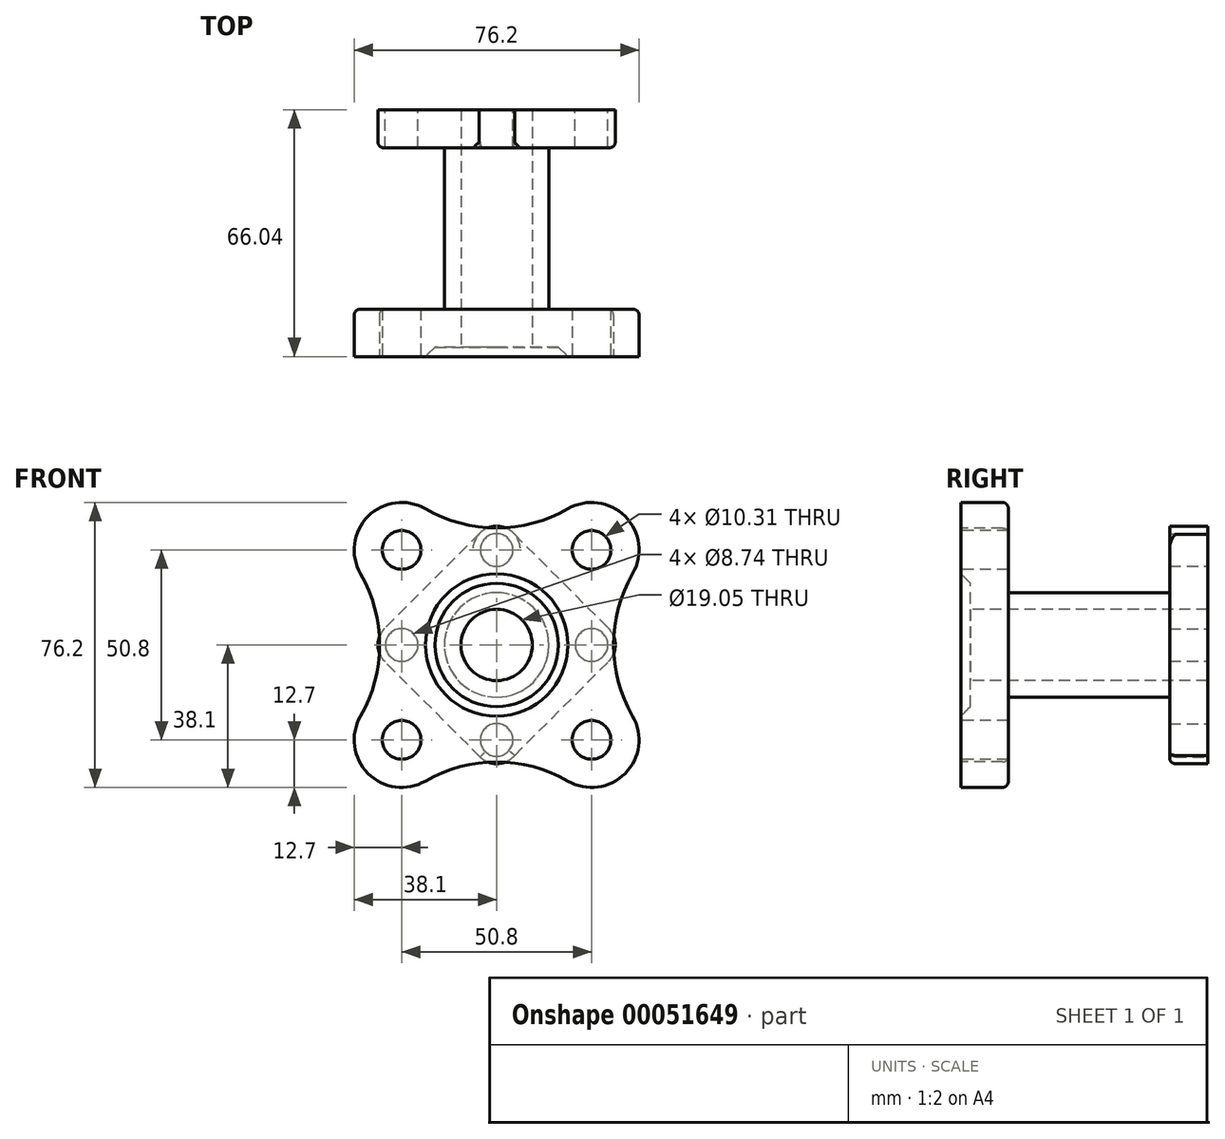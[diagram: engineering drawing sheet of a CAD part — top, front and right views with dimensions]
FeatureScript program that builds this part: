
annotation { "Feature Type Name" : "Feature", "Feature Type Description" : "" }
export const myFeature = defineFeature(function(context is Context, id is Id, definition is map)
    precondition{}
    {
        {
            var Q0;
            Q0=qCreatedBy(makeId("Front.planeOp"),FACE);
            var sketch = newSketch(context, id + "F0", { "sketchPlane" : qUnion([Q0])});
            skLineSegment(sketch, "E0.bottom", {"start": v(-25.4, 25.4) * mm, "end": v(25.4, 25.4) * mm, "construction": true});
            skLineSegment(sketch, "E0.top", {"start": v(-25.4, -25.4) * mm, "end": v(25.4, -25.4) * mm, "construction": true});
            skLineSegment(sketch, "E0.left", {"start": v(-25.4, 25.4) * mm, "end": v(-25.4, -25.4) * mm, "construction": true});
            skLineSegment(sketch, "E0.right", {"start": v(25.4, 25.4) * mm, "end": v(25.4, -25.4) * mm, "construction": true});
            skArc(sketch, "E1", {"start": v(19.05, -36.4) * mm, "mid": v(34.38, -34.38) * mm, "end": v(36.4, -19.05) * mm});
            skArc(sketch, "E2", {"start": v(-36.4, -19.05) * mm, "mid": v(-34.38, -34.38) * mm, "end": v(-19.05, -36.4) * mm});
            skCircle(sketch, "E3", {"center": v(-25.4, 25.4) * mm, "radius": 50.8 * mm, "construction": true});
            skCircle(sketch, "E4", {"center": v(-25.4, -25.4) * mm, "radius": 50.8 * mm, "construction": true});
            skArc(sketch, "E5", {"start": v(-36.4, -19.05) * mm, "mid": v(-31.3, 0) * mm, "end": v(-36.4, 19.05) * mm});
            skArc(sketch, "E6.MirrorCS", {"start": v(36.4, -19.05) * mm, "mid": v(31.3, 0) * mm, "end": v(36.4, 19.05) * mm});
            skCircle(sketch, "E7", {"center": v(25.4, 25.4) * mm, "radius": 50.8 * mm, "construction": true});
            skArc(sketch, "E8", {"start": v(-19.05, 36.4) * mm, "mid": v(0, 31.3) * mm, "end": v(19.05, 36.4) * mm});
            skArc(sketch, "E9.MirrorCS", {"start": v(-19.05, -36.4) * mm, "mid": v(0, -31.3) * mm, "end": v(19.05, -36.4) * mm});
            skArc(sketch, "E10.trimOffspring", {"start": v(-19.05, 36.4) * mm, "mid": v(-34.38, 34.38) * mm, "end": v(-36.4, 19.05) * mm});
            skArc(sketch, "E11.trimOffspring", {"start": v(36.4, 19.05) * mm, "mid": v(34.38, 34.38) * mm, "end": v(19.05, 36.4) * mm});
            skCircle(sketch, "E12", {"center": v(-25.4, 25.4) * mm, "radius": 5.16 * mm});
            skCircle(sketch, "E13", {"center": v(25.4, 25.4) * mm, "radius": 5.16 * mm});
            skCircle(sketch, "E14", {"center": v(-25.4, -25.4) * mm, "radius": 5.16 * mm});
            skCircle(sketch, "E15", {"center": v(25.4, -25.4) * mm, "radius": 5.16 * mm});
            skSolve(sketch);
        }
        {
            var Q0;
            Q0=makeQuery(id+"F0.imprint","IMPRINT",FACE,{"disambiguationData":[TD([[makeQuery(id+"F0.imprint","IMPRINT",EDGE,{"derivedFrom":sQuery(id+"F0.wireOp",EDGE,"E1")}),1.0]])]});
            extrude(context, id + "F1", {"entities" : qUnion([Q0]), "oppositeDirection" : true, "depth" : 12.7 * mm});
        }
        {
            var Q0;
            Q0=qCreatedBy(makeId("Front.planeOp"),FACE);
            cPlane(context, id + "F2", {"entities" : qUnion([Q0]), "cplaneType" : CPlaneType.OFFSET, "offset" : 66.04 * mm, "oppositeDirection" : true, "width" : 152.4 * mm, "height" : 152.4 * mm});
        }
        {
            var Q0;
            Q0=qCreatedBy(id+"F2.planeOp",FACE);
            var sketch = newSketch(context, id + "F3", { "sketchPlane" : qUnion([Q0])});
            skArc(sketch, "E16", {"start": v(4.78, 29.58) * mm, "mid": v(0.1, 31.75) * mm, "end": v(-4.64, 29.74) * mm});
            skArc(sketch, "E17", {"start": v(-29.89, 4.5) * mm, "mid": v(-31.75, 0) * mm, "end": v(-29.9, -4.5) * mm});
            skArc(sketch, "E18", {"start": v(-4.4, -29.97) * mm, "mid": v(0.29, -31.74) * mm, "end": v(4.8, -29.55) * mm});
            skArc(sketch, "E19", {"start": v(29.89, -4.5) * mm, "mid": v(31.75, 0) * mm, "end": v(29.89, 4.5) * mm});
            skLineSegment(sketch, "E20", {"start": v(-4.64, 29.74) * mm, "end": v(-29.89, 4.5) * mm});
            skLineSegment(sketch, "E21", {"start": v(-4.4, -29.97) * mm, "end": v(-29.9, -4.5) * mm});
            skLineSegment(sketch, "E22", {"start": v(4.78, 29.58) * mm, "end": v(29.89, 4.5) * mm});
            skLineSegment(sketch, "E23", {"start": v(4.8, -29.55) * mm, "end": v(29.89, -4.5) * mm});
            skSolve(sketch);
        }
        {
            var Q0;
            Q0=makeQuery(id+"F3.imprint","IMPRINT",FACE,{"disambiguationData":[TD([[makeQuery(id+"F3.imprint","IMPRINT",EDGE,{"derivedFrom":sQuery(id+"F3.wireOp",EDGE,"E16")}),1.0]])]});
            extrude(context, id + "F4", {"entities" : qUnion([Q0]), "depth" : 10.16 * mm});
        }
        {
            var Q0;
            Q0=makeQuery(id+"F1.opExtrude","CAP_FACE",FACE,{"disambiguationData":[OSD([sQuery(id+"F0.wireOp",EDGE,"E1"),sQuery(id+"F0.wireOp",EDGE,"E2"),sQuery(id+"F0.wireOp",EDGE,"E5"),sQuery(id+"F0.wireOp",EDGE,"E6.MirrorCS"),sQuery(id+"F0.wireOp",EDGE,"E8"),sQuery(id+"F0.wireOp",EDGE,"E9.MirrorCS"),sQuery(id+"F0.wireOp",EDGE,"E10.trimOffspring"),sQuery(id+"F0.wireOp",EDGE,"E11.trimOffspring"),sQuery(id+"F0.wireOp",EDGE,"E12"),sQuery(id+"F0.wireOp",EDGE,"E13"),sQuery(id+"F0.wireOp",EDGE,"E14"),sQuery(id+"F0.wireOp",EDGE,"E15")])],"isStart":false});
            var sketch = newSketch(context, id + "F5", { "sketchPlane" : qUnion([Q0])});
            skCircle(sketch, "E24", {"center": v(0, 0) * mm, "radius": 13.97 * mm});
            skSolve(sketch);
        }
        {
            var Q0;
            Q0 = qSketchRegion(id + "F5", true);
            extrude(context, id + "F6", {"entities" : qUnion([Q0]), "operationType" : NewBodyOperationType.ADD, "endBound" : BoundingType.UP_TO_NEXT, "depth" : 25.4 * mm});
        }
        {
            var Q0;
            Q0=makeQuery(id+"F4.opExtrude","CAP_FACE",FACE,{"disambiguationData":[OSD([sQuery(id+"F3.wireOp",EDGE,"E16"),sQuery(id+"F3.wireOp",EDGE,"E17"),sQuery(id+"F3.wireOp",EDGE,"E18"),sQuery(id+"F3.wireOp",EDGE,"E19"),sQuery(id+"F3.wireOp",EDGE,"E20"),sQuery(id+"F3.wireOp",EDGE,"E21"),sQuery(id+"F3.wireOp",EDGE,"E22"),sQuery(id+"F3.wireOp",EDGE,"E23")])],"isStart":true});
            var sketch = newSketch(context, id + "F7", { "sketchPlane" : qUnion([Q0])});
            skCircle(sketch, "E25", {"center": v(25.4, 0) * mm, "radius": 4.37 * mm});
            skCircle(sketch, "E26", {"center": v(0, -25.4) * mm, "radius": 4.37 * mm});
            skCircle(sketch, "E27", {"center": v(0, 25.4) * mm, "radius": 4.37 * mm});
            skCircle(sketch, "E28", {"center": v(-25.4, 0) * mm, "radius": 4.37 * mm});
            skSolve(sketch);
        }
        {
            var Q0;
            Q0=makeQuery(id+"F7.imprint","IMPRINT",FACE,{"disambiguationData":[TD([[makeQuery(id+"F7.imprint","IMPRINT",EDGE,{"derivedFrom":sQuery(id+"F7.wireOp",EDGE,"E25")}),1.0]])]});
            var Q1;
            Q1=makeQuery(id+"F7.imprint","IMPRINT",FACE,{"disambiguationData":[TD([[makeQuery(id+"F7.imprint","IMPRINT",EDGE,{"derivedFrom":sQuery(id+"F7.wireOp",EDGE,"E26")}),1.0]])]});
            var Q2;
            Q2=makeQuery(id+"F7.imprint","IMPRINT",FACE,{"disambiguationData":[TD([[makeQuery(id+"F7.imprint","IMPRINT",EDGE,{"derivedFrom":sQuery(id+"F7.wireOp",EDGE,"E27")}),1.0]])]});
            var Q3;
            Q3=makeQuery(id+"F7.imprint","IMPRINT",FACE,{"disambiguationData":[TD([[makeQuery(id+"F7.imprint","IMPRINT",EDGE,{"derivedFrom":sQuery(id+"F7.wireOp",EDGE,"E28")}),1.0]])]});
            extrude(context, id + "F8", {"entities" : qUnion([Q0, Q1, Q2, Q3]), "operationType" : NewBodyOperationType.REMOVE, "oppositeDirection" : true, "depth" : 12.7 * mm});
        }
        {
            var Q0;
            Q0=makeQuery(id+"F1.opExtrude","CAP_FACE",FACE,{"disambiguationData":[OSD([sQuery(id+"F0.wireOp",EDGE,"E1"),sQuery(id+"F0.wireOp",EDGE,"E2"),sQuery(id+"F0.wireOp",EDGE,"E5"),sQuery(id+"F0.wireOp",EDGE,"E6.MirrorCS"),sQuery(id+"F0.wireOp",EDGE,"E8"),sQuery(id+"F0.wireOp",EDGE,"E9.MirrorCS"),sQuery(id+"F0.wireOp",EDGE,"E10.trimOffspring"),sQuery(id+"F0.wireOp",EDGE,"E11.trimOffspring"),sQuery(id+"F0.wireOp",EDGE,"E12"),sQuery(id+"F0.wireOp",EDGE,"E13"),sQuery(id+"F0.wireOp",EDGE,"E14"),sQuery(id+"F0.wireOp",EDGE,"E15")])],"isStart":true});
            var sketch = newSketch(context, id + "F9", { "sketchPlane" : qUnion([Q0])});
            skCircle(sketch, "E29", {"center": v(0, 0) * mm, "radius": 9.53 * mm});
            skSolve(sketch);
        }
        {
            var Q0;
            Q0 = qSketchRegion(id + "F9", true);
            extrude(context, id + "F10", {"entities" : qUnion([Q0]), "operationType" : NewBodyOperationType.REMOVE, "endBound" : BoundingType.THROUGH_ALL, "oppositeDirection" : true, "depth" : 25.4 * mm});
        }
        {
            var Q0;
            Q0=qCreatedBy(makeId("Top.planeOp"),FACE);
            var sketch = newSketch(context, id + "F11", { "sketchPlane" : qUnion([Q0])});
            skLineSegment(sketch, "E30", {"start": v(-16.5, 2.54) * mm, "end": v(0, 2.54) * mm});
            skLineSegment(sketch, "E31", {"start": v(0, 2.54) * mm, "end": v(0, 0) * mm});
            skLineSegment(sketch, "E32", {"start": v(0, 0) * mm, "end": v(-19.05, 0) * mm});
            skLineSegment(sketch, "E33", {"start": v(-19.05, 0) * mm, "end": v(-16.5, 2.54) * mm});
            skSolve(sketch);
        }
        {
            var Q0;
            Q0 = qSketchRegion(id + "F11", true);
            var Q1;
            Q1=sQuery(id+"F11.wireOp",EDGE,"E31");
            revolve(context, id + "F12", {"operationType" : NewBodyOperationType.REMOVE, "entities" : qUnion([Q0]), "axis" : qUnion([Q1]), "revolveType" : RevolveType.FULL, "oppositeDirection" : true});
        }
        {
            var Q0;
            Q0=makeQuery(id+"F4.opExtrude","CAP_EDGE",EDGE,{"disambiguationData":[OSD([sQuery(id+"F3.wireOp",EDGE,"E20")])],"isStart":false});
            var Q1;
            Q1=makeQuery(id+"F4.opExtrude","CAP_EDGE",EDGE,{"disambiguationData":[OSD([sQuery(id+"F3.wireOp",EDGE,"E22")])],"isStart":false});
            var Q2;
            Q2=makeQuery(id+"F4.opExtrude","CAP_EDGE",EDGE,{"disambiguationData":[OSD([sQuery(id+"F3.wireOp",EDGE,"E18")])],"isStart":false});
            var Q3;
            Q3=makeQuery(id+"F6.opExtrude","CAP_EDGE",EDGE,{"disambiguationData":[OSD([sQuery(id+"F5.wireOp",EDGE,"E24")])],"isStart":false});
            var Q4;
            Q4=makeQuery(id+"F6.opExtrude","CAP_EDGE",EDGE,{"disambiguationData":[OSD([sQuery(id+"F5.wireOp",EDGE,"E24")])],"isStart":true});
            var Q5;
            Q5=makeQuery(id+"F1.opExtrude","CAP_EDGE",EDGE,{"disambiguationData":[OSD([sQuery(id+"F0.wireOp",EDGE,"E9.MirrorCS")])],"isStart":false});
            fillet(context, id + "F13", {"entities" : qUnion([Q0, Q1, Q2, Q3, Q4, Q5]), "radius" : 1.52 * mm, "tangentPropagation" : true, "allowEdgeOverflow" : false});
        }
    });
